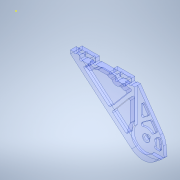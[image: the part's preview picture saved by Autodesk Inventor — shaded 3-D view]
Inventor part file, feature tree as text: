
AUTODESK INVENTOR PART (.ipt)
format: ipt  version: 2020.2 (Build 242310000, 310)  size: 809,472 bytes
history: native  units: mm
features: extrude x17, sketch x16, projected_geometry x15, fillet x4, other x1
ambient origin geometry x8: Origin, YZ Plane, XZ Plane, XY Plane, X Axis, Y Axis, Z Axis, Center Point
bodies: Body1 (feature_tree)
feature tree (53):
  other  "ソリッド1"
  sketch  "スケッチ1"
  extrude  "押し出し1"  Depth=5.0mm
  extrude  "押し出し2"  Depth=3.0mm
  extrude  "押し出し3"  Depth=5.0mm
  extrude  "押し出し4"  Depth=3.0mm
  sketch  "スケッチ4"
  sketch  "スケッチ6"
  sketch  "スケッチ8"
  extrude  "押し出し10"  Depth=3.0mm
  extrude  "押し出し11"  Depth=5.0mm
  extrude  "押し出し12"  Depth=1.0mm
  extrude  "押し出し13"  Depth=5.0mm
  extrude  "押し出し14"  Depth=5.0mm
  sketch  "スケッチ9"
  extrude  "押し出し15"  Depth=2.0mm
  extrude  "押し出し16"  Depth=2.0mm
  extrude  "押し出し17"  Depth=2.0mm
  sketch  "スケッチ11"
  fillet  "フィレット1"  Radius=2.0mm
  extrude  "押し出し18"  Depth=2.0mm
  fillet  "フィレット2"  Radius=2.0mm
  sketch  "スケッチ13"
  extrude  "押し出し19"  Depth=2.0mm
  extrude  "押し出し20"  Depth=2.0mm
  fillet  "フィレット3"  Radius=2.0mm
  extrude  "押し出し21"  Depth=2.0mm
  fillet  "フィレット4"  Radius=2.0mm
  sketch  "スケッチ17"
  extrude  "押し出し22"  Depth=2.0mm
  sketch  "スケッチ2"
  projected_geometry  "投影ループ1"
  sketch  "スケッチ3"
  projected_geometry  "投影ループ2"
  projected_geometry  "投影ループ3"
  projected_geometry  "投影ループ5"
  projected_geometry  "投影ループ6"
  projected_geometry  "投影ループ9"
  sketch  "スケッチ10"
  projected_geometry  "投影ループ10"
  projected_geometry  "投影ループ11"
  projected_geometry  "投影ループ12"
  sketch  "スケッチ12"
  projected_geometry  "投影ループ13"
  sketch  "スケッチ14"
  projected_geometry  "投影ループ14"
  sketch  "スケッチ15"
  projected_geometry  "投影ループ15"
  sketch  "スケッチ16"
  projected_geometry  "投影ループ16"
  projected_geometry  "投影ループ17"
  projected_geometry  "投影ループ18"
  sketch  "スケッチ18"
